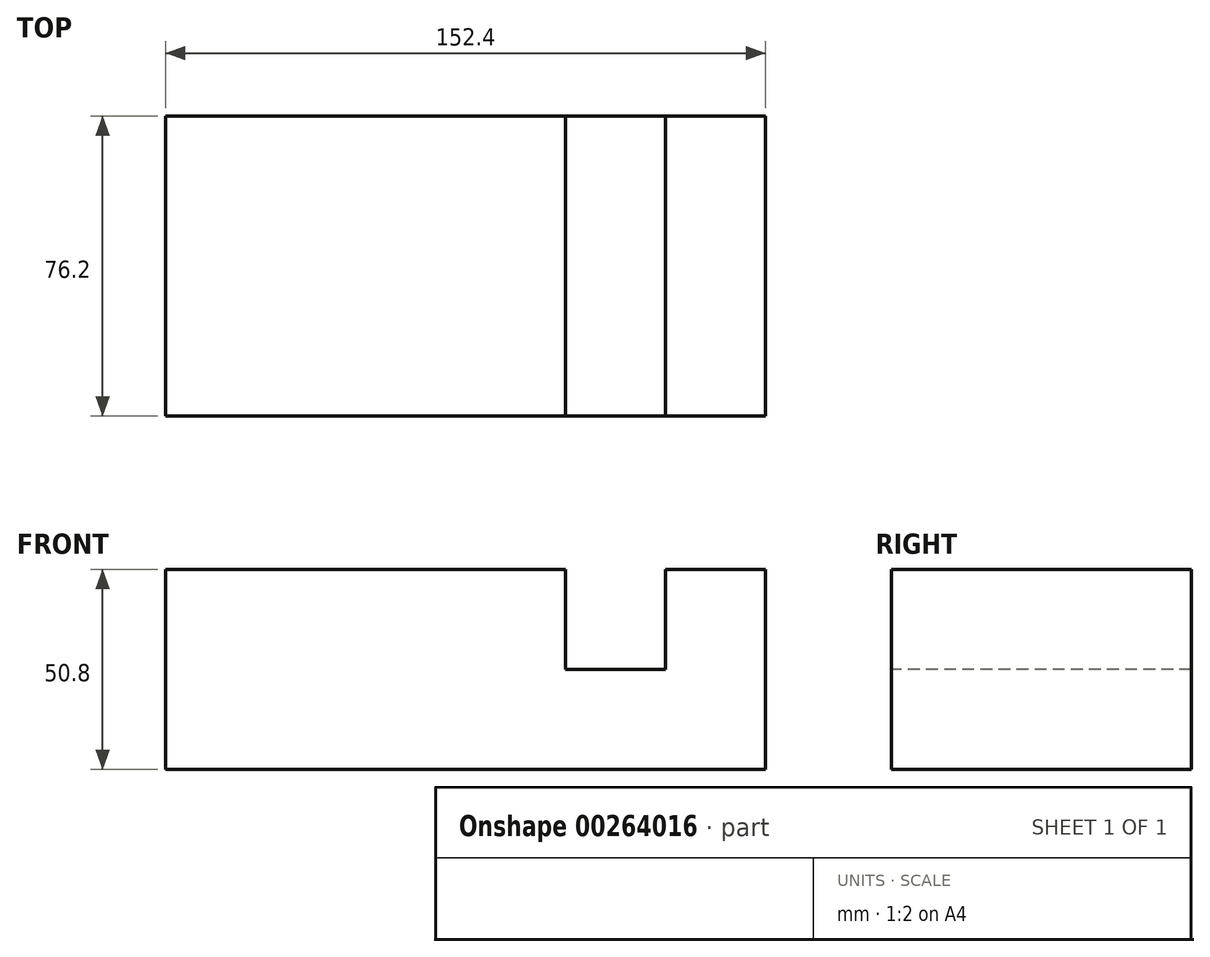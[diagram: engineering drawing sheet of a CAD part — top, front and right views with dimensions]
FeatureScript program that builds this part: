
annotation { "Feature Type Name" : "Feature", "Feature Type Description" : "" }
export const myFeature = defineFeature(function(context is Context, id is Id, definition is map)
    precondition{}
    {
        {
            var Q0;
            Q0=qCreatedBy(makeId("Front.planeOp"),FACE);
            var sketch = newSketch(context, id + "F0", { "sketchPlane" : qUnion([Q0])});
            skLineSegment(sketch, "E0", {"start": v(-101.6, 0) * mm, "end": v(-101.6, 50.8) * mm});
            skLineSegment(sketch, "E1", {"start": v(-101.6, 50.8) * mm, "end": v(0, 50.8) * mm});
            skLineSegment(sketch, "E2", {"start": v(0, 50.8) * mm, "end": v(0, 25.4) * mm});
            skLineSegment(sketch, "E3", {"start": v(0, 25.4) * mm, "end": v(25.4, 25.4) * mm});
            skLineSegment(sketch, "E4", {"start": v(25.4, 25.4) * mm, "end": v(25.4, 50.8) * mm});
            skLineSegment(sketch, "E5", {"start": v(25.4, 50.8) * mm, "end": v(50.8, 50.8) * mm});
            skLineSegment(sketch, "E6", {"start": v(50.8, 50.8) * mm, "end": v(50.8, 0) * mm});
            skLineSegment(sketch, "E7", {"start": v(50.8, 0) * mm, "end": v(-101.6, 0) * mm});
            skSolve(sketch);
        }
        {
            var Q0;
            Q0=makeQuery(id+"F0.imprint","IMPRINT",FACE,{"disambiguationData":[TD([[makeQuery(id+"F0.imprint","IMPRINT",EDGE,{"derivedFrom":sQuery(id+"F0.wireOp",EDGE,"E0")}),-1.0]])]});
            extrude(context, id + "F1", {"entities" : qUnion([Q0]), "oppositeDirection" : true, "depth" : 38.1 * mm});
        }
        {
            var Q0;
            Q0=makeQuery(id+"F1.opExtrude","CAP_FACE",FACE,{"disambiguationData":[OSD([sQuery(id+"F0.wireOp",EDGE,"E0"),sQuery(id+"F0.wireOp",EDGE,"E1"),sQuery(id+"F0.wireOp",EDGE,"E2"),sQuery(id+"F0.wireOp",EDGE,"E3"),sQuery(id+"F0.wireOp",EDGE,"E4"),sQuery(id+"F0.wireOp",EDGE,"E5"),sQuery(id+"F0.wireOp",EDGE,"E6"),sQuery(id+"F0.wireOp",EDGE,"E7")])],"isStart":true});
            extrude(context, id + "F2", {"entities" : qUnion([Q0]), "operationType" : NewBodyOperationType.ADD, "depth" : 38.1 * mm});
        }
    });
